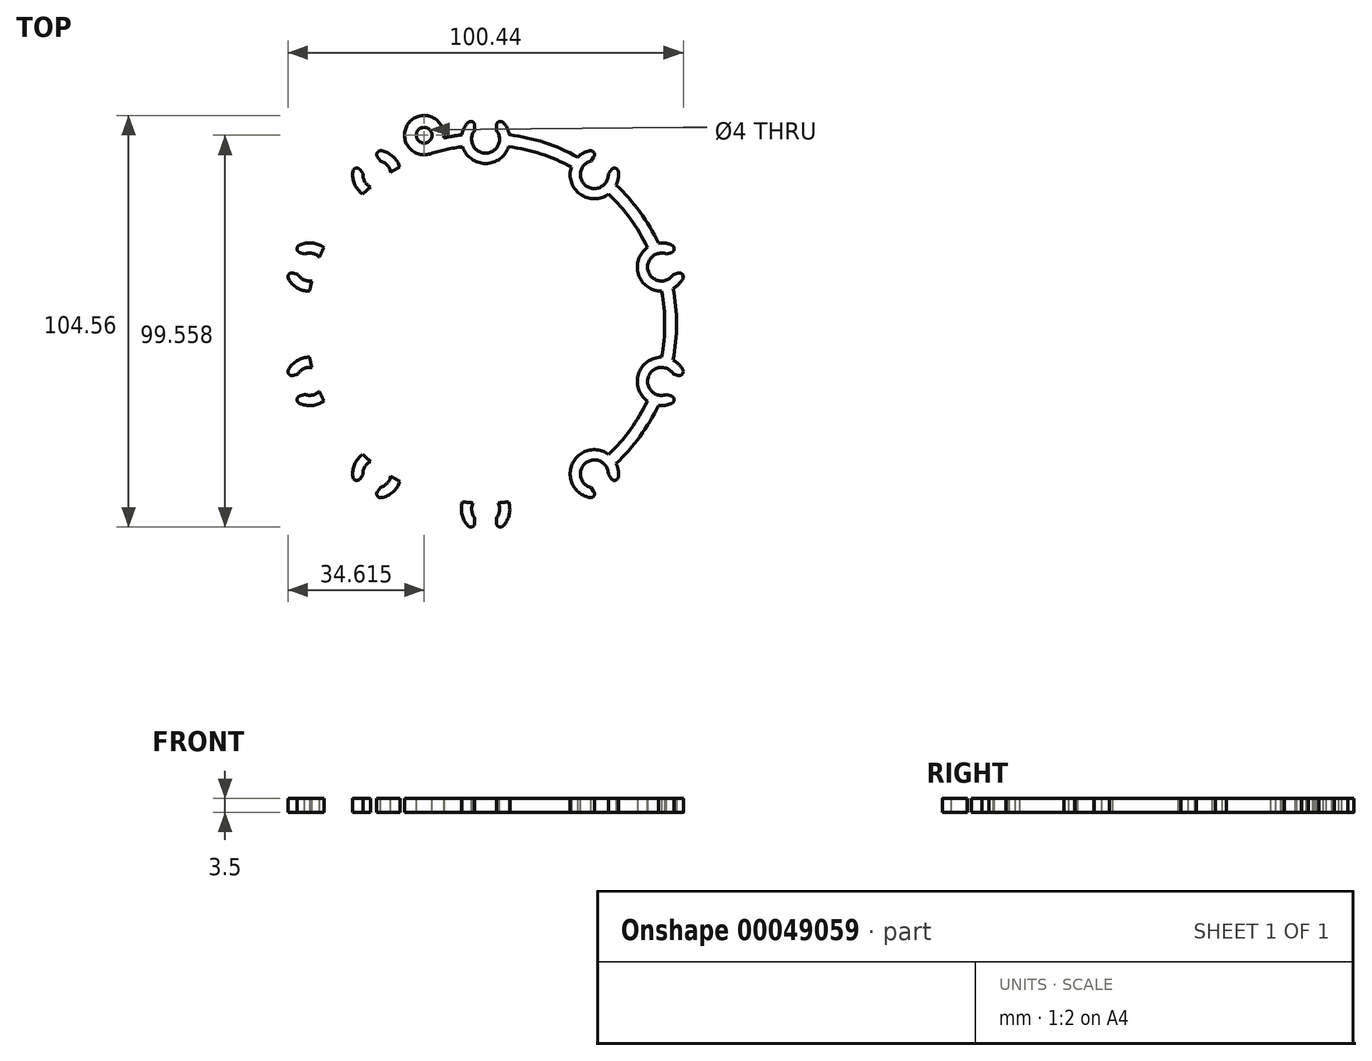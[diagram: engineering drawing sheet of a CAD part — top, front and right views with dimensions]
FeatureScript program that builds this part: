
annotation { "Feature Type Name" : "Feature", "Feature Type Description" : "" }
export const myFeature = defineFeature(function(context is Context, id is Id, definition is map)
    precondition{}
    {
        {
            var Q0;
            Q0=qCreatedBy(makeId("Top.planeOp"),FACE);
            var sketch = newSketch(context, id + "F0", { "sketchPlane" : qUnion([Q0])});
            skLineSegment(sketch, "E0", {"start": v(0, 0) * mm, "end": v(0, 47) * mm, "construction": true});
            skCircle(sketch, "E1", {"center": v(0, 47) * mm, "radius": 15 * mm, "construction": true});
            skCircle(sketch, "E2.1.0", {"center": v(-27.63, 38.02) * mm, "radius": 15 * mm, "construction": true});
            skCircle(sketch, "E2.2.0", {"center": v(-44.7, 14.52) * mm, "radius": 15 * mm, "construction": true});
            skCircle(sketch, "E2.3.0", {"center": v(-44.7, -14.52) * mm, "radius": 15 * mm, "construction": true});
            skCircle(sketch, "E2.4.0", {"center": v(-27.63, -38.02) * mm, "radius": 15 * mm, "construction": true});
            skCircle(sketch, "E2.5.0", {"center": v(0, -47) * mm, "radius": 15 * mm, "construction": true});
            skCircle(sketch, "E2.6.0", {"center": v(27.63, -38.02) * mm, "radius": 15 * mm, "construction": true});
            skCircle(sketch, "E2.7.0", {"center": v(44.7, -14.52) * mm, "radius": 15 * mm, "construction": true});
            skCircle(sketch, "E2.8.0", {"center": v(44.7, 14.52) * mm, "radius": 15 * mm, "construction": true});
            skCircle(sketch, "E2.9.0", {"center": v(27.63, 38.02) * mm, "radius": 15 * mm, "construction": true});
            skPoint(sketch, "E2.center", {"position": v(0, 0) * mm});
            skCircle(sketch, "E3", {"center": v(0, 47) * mm, "radius": 6.15 * mm});
            skCircle(sketch, "E4.1.0", {"center": v(-27.63, 38.02) * mm, "radius": 6.15 * mm});
            skCircle(sketch, "E4.2.0", {"center": v(-44.7, 14.52) * mm, "radius": 6.15 * mm});
            skCircle(sketch, "E4.3.0", {"center": v(-44.7, -14.52) * mm, "radius": 6.15 * mm});
            skCircle(sketch, "E4.4.0", {"center": v(-27.63, -38.02) * mm, "radius": 6.15 * mm});
            skCircle(sketch, "E4.5.0", {"center": v(0, -47) * mm, "radius": 6.15 * mm});
            skCircle(sketch, "E4.6.0", {"center": v(27.63, -38.02) * mm, "radius": 6.15 * mm});
            skCircle(sketch, "E4.7.0", {"center": v(44.7, -14.52) * mm, "radius": 6.15 * mm});
            skCircle(sketch, "E4.8.0", {"center": v(44.7, 14.52) * mm, "radius": 6.15 * mm});
            skCircle(sketch, "E4.9.0", {"center": v(27.63, 38.02) * mm, "radius": 6.15 * mm});
            skCircle(sketch, "E5", {"center": v(0, 0) * mm, "radius": 45.5 * mm});
            skCircle(sketch, "E6", {"center": v(0, 0) * mm, "radius": 48.5 * mm});
            skLineSegment(sketch, "E7", {"start": v(0, 0) * mm, "end": v(-15.6, 48.03) * mm, "construction": true});
            skCircle(sketch, "E8", {"center": v(-15.6, 48.03) * mm, "radius": 5 * mm});
            skSolve(sketch);
        }
        {
            var Q0;
            {var subQ0=sQuery(id+"F0.wireOp",EDGE,"E6");var subQ1=sQuery(id+"F0.wireOp",EDGE,"E4.2.0");var subQ3=makeQuery(id+"F0.imprint","INTERSECT",VERTEX,{"disambiguationData":[OD(0.0)],"derivedFrom":[subQ1,subQ0]});Q0=makeQuery(id+"F0.imprint","IMPRINT",FACE,{"disambiguationData":[TD([[makeQuery(id+"F0.imprint","IMPRINT",EDGE,{"disambiguationData":[TD([[subQ3,1.0]])],"derivedFrom":subQ1}),1.0]])]});}
            var Q1;
            {var subQ0=sQuery(id+"F0.wireOp",EDGE,"E6");var subQ1=sQuery(id+"F0.wireOp",EDGE,"E4.3.0");var subQ3=makeQuery(id+"F0.imprint","INTERSECT",VERTEX,{"disambiguationData":[OD(0.0)],"derivedFrom":[subQ1,subQ0]});Q1=makeQuery(id+"F0.imprint","IMPRINT",FACE,{"disambiguationData":[TD([[makeQuery(id+"F0.imprint","IMPRINT",EDGE,{"disambiguationData":[TD([[subQ3,1.0]])],"derivedFrom":subQ1}),1.0]])]});}
            var Q2;
            {var subQ1=sQuery(id+"F0.wireOp",EDGE,"E4.3.0");var subQ4=sQuery(id+"F0.wireOp",EDGE,"E6");var subQ6=makeQuery(id+"F0.imprint","INTERSECT",VERTEX,{"disambiguationData":[OD(0.0)],"derivedFrom":[subQ1,subQ4]});Q2=makeQuery(id+"F0.imprint","IMPRINT",FACE,{"disambiguationData":[TD([[makeQuery(id+"F0.imprint","IMPRINT",EDGE,{"disambiguationData":[TD([[subQ6,-1.0]])],"derivedFrom":subQ1}),1.0]])]});}
            var Q3;
            {var subQ3=sQuery(id+"F0.wireOp",EDGE,"E4.2.0");var subQ5=sQuery(id+"F0.wireOp",EDGE,"E6");var subQ7=makeQuery(id+"F0.imprint","INTERSECT",VERTEX,{"disambiguationData":[OD(0.0)],"derivedFrom":[subQ3,subQ5]});Q3=makeQuery(id+"F0.imprint","IMPRINT",FACE,{"disambiguationData":[TD([[makeQuery(id+"F0.imprint","IMPRINT",EDGE,{"disambiguationData":[TD([[subQ7,-1.0]])],"derivedFrom":subQ3}),-1.0]])]});}
            var Q4;
            {var subQ0=sQuery(id+"F0.wireOp",EDGE,"E5");var subQ1=sQuery(id+"F0.wireOp",EDGE,"E4.2.0");var subQ3=makeQuery(id+"F0.imprint","INTERSECT",VERTEX,{"disambiguationData":[OD(0.0)],"derivedFrom":[subQ1,subQ0]});Q4=makeQuery(id+"F0.imprint","IMPRINT",FACE,{"disambiguationData":[TD([[makeQuery(id+"F0.imprint","IMPRINT",EDGE,{"disambiguationData":[TD([[subQ3,-1.0]])],"derivedFrom":subQ1}),1.0]])]});}
            var Q5;
            {var subQ3=sQuery(id+"F0.wireOp",EDGE,"E4.3.0");var subQ5=sQuery(id+"F0.wireOp",EDGE,"E6");var subQ7=makeQuery(id+"F0.imprint","INTERSECT",VERTEX,{"disambiguationData":[OD(0.0)],"derivedFrom":[subQ3,subQ5]});Q5=makeQuery(id+"F0.imprint","IMPRINT",FACE,{"disambiguationData":[TD([[makeQuery(id+"F0.imprint","IMPRINT",EDGE,{"disambiguationData":[TD([[subQ7,-1.0]])],"derivedFrom":subQ3}),-1.0]])]});}
            var Q6;
            {var subQ0=sQuery(id+"F0.wireOp",EDGE,"E5");var subQ1=sQuery(id+"F0.wireOp",EDGE,"E4.4.0");var subQ3=makeQuery(id+"F0.imprint","INTERSECT",VERTEX,{"disambiguationData":[OD(0.0)],"derivedFrom":[subQ1,subQ0]});Q6=makeQuery(id+"F0.imprint","IMPRINT",FACE,{"disambiguationData":[TD([[makeQuery(id+"F0.imprint","IMPRINT",EDGE,{"disambiguationData":[TD([[subQ3,-1.0]])],"derivedFrom":subQ1}),1.0]])]});}
            var Q7;
            {var subQ0=sQuery(id+"F0.wireOp",EDGE,"E6");var subQ1=sQuery(id+"F0.wireOp",EDGE,"E4.4.0");var subQ3=makeQuery(id+"F0.imprint","INTERSECT",VERTEX,{"disambiguationData":[OD(0.0)],"derivedFrom":[subQ1,subQ0]});Q7=makeQuery(id+"F0.imprint","IMPRINT",FACE,{"disambiguationData":[TD([[makeQuery(id+"F0.imprint","IMPRINT",EDGE,{"disambiguationData":[TD([[subQ3,-1.0]])],"derivedFrom":subQ1}),1.0]])]});}
            var Q8;
            {var subQ0=sQuery(id+"F0.wireOp",EDGE,"E6");var subQ1=sQuery(id+"F0.wireOp",EDGE,"E4.4.0");var subQ3=makeQuery(id+"F0.imprint","INTERSECT",VERTEX,{"disambiguationData":[OD(0.0)],"derivedFrom":[subQ1,subQ0]});Q8=makeQuery(id+"F0.imprint","IMPRINT",FACE,{"disambiguationData":[TD([[makeQuery(id+"F0.imprint","IMPRINT",EDGE,{"disambiguationData":[TD([[subQ3,1.0]])],"derivedFrom":subQ1}),1.0]])]});}
            var Q9;
            {var subQ0=sQuery(id+"F0.wireOp",EDGE,"E6");var subQ3=sQuery(id+"F0.wireOp",EDGE,"E4.4.0");var subQ4=makeQuery(id+"F0.imprint","INTERSECT",VERTEX,{"disambiguationData":[OD(0.0)],"derivedFrom":[subQ3,subQ0]});Q9=makeQuery(id+"F0.imprint","IMPRINT",FACE,{"disambiguationData":[TD([[makeQuery(id+"F0.imprint","IMPRINT",EDGE,{"disambiguationData":[TD([[subQ4,-1.0]])],"derivedFrom":subQ3}),-1.0]])]});}
            var Q10;
            {var subQ0=sQuery(id+"F0.wireOp",EDGE,"E5");var subQ1=sQuery(id+"F0.wireOp",EDGE,"E4.5.0");var subQ3=makeQuery(id+"F0.imprint","INTERSECT",VERTEX,{"disambiguationData":[OD(0.0)],"derivedFrom":[subQ1,subQ0]});Q10=makeQuery(id+"F0.imprint","IMPRINT",FACE,{"disambiguationData":[TD([[makeQuery(id+"F0.imprint","IMPRINT",EDGE,{"disambiguationData":[TD([[subQ3,-1.0]])],"derivedFrom":subQ1}),1.0]])]});}
            var Q11;
            {var subQ0=sQuery(id+"F0.wireOp",EDGE,"E6");var subQ1=sQuery(id+"F0.wireOp",EDGE,"E4.5.0");var subQ3=makeQuery(id+"F0.imprint","INTERSECT",VERTEX,{"disambiguationData":[OD(0.0)],"derivedFrom":[subQ1,subQ0]});Q11=makeQuery(id+"F0.imprint","IMPRINT",FACE,{"disambiguationData":[TD([[makeQuery(id+"F0.imprint","IMPRINT",EDGE,{"disambiguationData":[TD([[subQ3,1.0]])],"derivedFrom":subQ1}),1.0]])]});}
            var Q12;
            {var subQ0=sQuery(id+"F0.wireOp",EDGE,"E6");var subQ1=sQuery(id+"F0.wireOp",EDGE,"E4.5.0");var subQ3=makeQuery(id+"F0.imprint","INTERSECT",VERTEX,{"disambiguationData":[OD(0.0)],"derivedFrom":[subQ1,subQ0]});Q12=makeQuery(id+"F0.imprint","IMPRINT",FACE,{"disambiguationData":[TD([[makeQuery(id+"F0.imprint","IMPRINT",EDGE,{"disambiguationData":[TD([[subQ3,-1.0]])],"derivedFrom":subQ1}),1.0]])]});}
            var Q13;
            {var subQ0=sQuery(id+"F0.wireOp",EDGE,"E6");var subQ3=sQuery(id+"F0.wireOp",EDGE,"E4.5.0");var subQ4=makeQuery(id+"F0.imprint","INTERSECT",VERTEX,{"disambiguationData":[OD(0.0)],"derivedFrom":[subQ3,subQ0]});Q13=makeQuery(id+"F0.imprint","IMPRINT",FACE,{"disambiguationData":[TD([[makeQuery(id+"F0.imprint","IMPRINT",EDGE,{"disambiguationData":[TD([[subQ4,-1.0]])],"derivedFrom":subQ3}),-1.0]])]});}
            var Q14;
            {var subQ0=sQuery(id+"F0.wireOp",EDGE,"E5");var subQ1=sQuery(id+"F0.wireOp",EDGE,"E4.6.0");var subQ3=makeQuery(id+"F0.imprint","INTERSECT",VERTEX,{"disambiguationData":[OD(0.0)],"derivedFrom":[subQ1,subQ0]});Q14=makeQuery(id+"F0.imprint","IMPRINT",FACE,{"disambiguationData":[TD([[makeQuery(id+"F0.imprint","IMPRINT",EDGE,{"disambiguationData":[TD([[subQ3,-1.0]])],"derivedFrom":subQ1}),1.0]])]});}
            var Q15;
            {var subQ0=sQuery(id+"F0.wireOp",EDGE,"E6");var subQ1=sQuery(id+"F0.wireOp",EDGE,"E4.6.0");var subQ3=makeQuery(id+"F0.imprint","INTERSECT",VERTEX,{"disambiguationData":[OD(0.0)],"derivedFrom":[subQ1,subQ0]});Q15=makeQuery(id+"F0.imprint","IMPRINT",FACE,{"disambiguationData":[TD([[makeQuery(id+"F0.imprint","IMPRINT",EDGE,{"disambiguationData":[TD([[subQ3,-1.0]])],"derivedFrom":subQ1}),1.0]])]});}
            var Q16;
            {var subQ0=sQuery(id+"F0.wireOp",EDGE,"E6");var subQ1=sQuery(id+"F0.wireOp",EDGE,"E4.6.0");var subQ3=makeQuery(id+"F0.imprint","INTERSECT",VERTEX,{"disambiguationData":[OD(0.0)],"derivedFrom":[subQ1,subQ0]});Q16=makeQuery(id+"F0.imprint","IMPRINT",FACE,{"disambiguationData":[TD([[makeQuery(id+"F0.imprint","IMPRINT",EDGE,{"disambiguationData":[TD([[subQ3,1.0]])],"derivedFrom":subQ1}),1.0]])]});}
            var Q17;
            {var subQ0=sQuery(id+"F0.wireOp",EDGE,"E6");var subQ3=sQuery(id+"F0.wireOp",EDGE,"E4.6.0");var subQ4=makeQuery(id+"F0.imprint","INTERSECT",VERTEX,{"disambiguationData":[OD(0.0)],"derivedFrom":[subQ3,subQ0]});Q17=makeQuery(id+"F0.imprint","IMPRINT",FACE,{"disambiguationData":[TD([[makeQuery(id+"F0.imprint","IMPRINT",EDGE,{"disambiguationData":[TD([[subQ4,-1.0]])],"derivedFrom":subQ3}),-1.0]])]});}
            var Q18;
            {var subQ0=sQuery(id+"F0.wireOp",EDGE,"E5");var subQ1=sQuery(id+"F0.wireOp",EDGE,"E4.7.0");var subQ3=makeQuery(id+"F0.imprint","INTERSECT",VERTEX,{"disambiguationData":[OD(0.0)],"derivedFrom":[subQ1,subQ0]});Q18=makeQuery(id+"F0.imprint","IMPRINT",FACE,{"disambiguationData":[TD([[makeQuery(id+"F0.imprint","IMPRINT",EDGE,{"disambiguationData":[TD([[subQ3,-1.0]])],"derivedFrom":subQ1}),1.0]])]});}
            var Q19;
            {var subQ0=sQuery(id+"F0.wireOp",EDGE,"E6");var subQ1=sQuery(id+"F0.wireOp",EDGE,"E4.7.0");var subQ3=makeQuery(id+"F0.imprint","INTERSECT",VERTEX,{"disambiguationData":[OD(0.0)],"derivedFrom":[subQ1,subQ0]});Q19=makeQuery(id+"F0.imprint","IMPRINT",FACE,{"disambiguationData":[TD([[makeQuery(id+"F0.imprint","IMPRINT",EDGE,{"disambiguationData":[TD([[subQ3,-1.0]])],"derivedFrom":subQ1}),1.0]])]});}
            var Q20;
            {var subQ0=sQuery(id+"F0.wireOp",EDGE,"E6");var subQ1=sQuery(id+"F0.wireOp",EDGE,"E4.7.0");var subQ3=makeQuery(id+"F0.imprint","INTERSECT",VERTEX,{"disambiguationData":[OD(0.0)],"derivedFrom":[subQ1,subQ0]});Q20=makeQuery(id+"F0.imprint","IMPRINT",FACE,{"disambiguationData":[TD([[makeQuery(id+"F0.imprint","IMPRINT",EDGE,{"disambiguationData":[TD([[subQ3,1.0]])],"derivedFrom":subQ1}),1.0]])]});}
            var Q21;
            {var subQ0=sQuery(id+"F0.wireOp",EDGE,"E6");var subQ3=sQuery(id+"F0.wireOp",EDGE,"E4.7.0");var subQ4=makeQuery(id+"F0.imprint","INTERSECT",VERTEX,{"disambiguationData":[OD(0.0)],"derivedFrom":[subQ3,subQ0]});Q21=makeQuery(id+"F0.imprint","IMPRINT",FACE,{"disambiguationData":[TD([[makeQuery(id+"F0.imprint","IMPRINT",EDGE,{"disambiguationData":[TD([[subQ4,-1.0]])],"derivedFrom":subQ3}),-1.0]])]});}
            var Q22;
            {var subQ0=sQuery(id+"F0.wireOp",EDGE,"E5");var subQ1=sQuery(id+"F0.wireOp",EDGE,"E4.8.0");var subQ3=makeQuery(id+"F0.imprint","INTERSECT",VERTEX,{"disambiguationData":[OD(0.0)],"derivedFrom":[subQ1,subQ0]});Q22=makeQuery(id+"F0.imprint","IMPRINT",FACE,{"disambiguationData":[TD([[makeQuery(id+"F0.imprint","IMPRINT",EDGE,{"disambiguationData":[TD([[subQ3,-1.0]])],"derivedFrom":subQ1}),1.0]])]});}
            var Q23;
            {var subQ0=sQuery(id+"F0.wireOp",EDGE,"E6");var subQ1=sQuery(id+"F0.wireOp",EDGE,"E4.8.0");var subQ3=makeQuery(id+"F0.imprint","INTERSECT",VERTEX,{"disambiguationData":[OD(0.0)],"derivedFrom":[subQ1,subQ0]});Q23=makeQuery(id+"F0.imprint","IMPRINT",FACE,{"disambiguationData":[TD([[makeQuery(id+"F0.imprint","IMPRINT",EDGE,{"disambiguationData":[TD([[subQ3,1.0]])],"derivedFrom":subQ1}),1.0]])]});}
            var Q24;
            {var subQ0=sQuery(id+"F0.wireOp",EDGE,"E6");var subQ1=sQuery(id+"F0.wireOp",EDGE,"E4.2.0");var subQ3=makeQuery(id+"F0.imprint","INTERSECT",VERTEX,{"disambiguationData":[OD(0.0)],"derivedFrom":[subQ1,subQ0]});Q24=makeQuery(id+"F0.imprint","IMPRINT",FACE,{"disambiguationData":[TD([[makeQuery(id+"F0.imprint","IMPRINT",EDGE,{"disambiguationData":[TD([[subQ3,-1.0]])],"derivedFrom":subQ1}),1.0]])]});}
            var Q25;
            {var subQ0=sQuery(id+"F0.wireOp",EDGE,"E6");var subQ3=sQuery(id+"F0.wireOp",EDGE,"E4.1.0");var subQ4=makeQuery(id+"F0.imprint","INTERSECT",VERTEX,{"disambiguationData":[OD(0.0)],"derivedFrom":[subQ3,subQ0]});Q25=makeQuery(id+"F0.imprint","IMPRINT",FACE,{"disambiguationData":[TD([[makeQuery(id+"F0.imprint","IMPRINT",EDGE,{"disambiguationData":[TD([[subQ4,-1.0]])],"derivedFrom":subQ3}),-1.0]])]});}
            var Q26;
            {var subQ0=sQuery(id+"F0.wireOp",EDGE,"E6");var subQ1=sQuery(id+"F0.wireOp",EDGE,"E4.1.0");var subQ3=makeQuery(id+"F0.imprint","INTERSECT",VERTEX,{"disambiguationData":[OD(0.0)],"derivedFrom":[subQ1,subQ0]});Q26=makeQuery(id+"F0.imprint","IMPRINT",FACE,{"disambiguationData":[TD([[makeQuery(id+"F0.imprint","IMPRINT",EDGE,{"disambiguationData":[TD([[subQ3,1.0]])],"derivedFrom":subQ1}),1.0]])]});}
            var Q27;
            {var subQ0=sQuery(id+"F0.wireOp",EDGE,"E6");var subQ1=sQuery(id+"F0.wireOp",EDGE,"E4.1.0");var subQ3=makeQuery(id+"F0.imprint","INTERSECT",VERTEX,{"disambiguationData":[OD(0.0)],"derivedFrom":[subQ1,subQ0]});Q27=makeQuery(id+"F0.imprint","IMPRINT",FACE,{"disambiguationData":[TD([[makeQuery(id+"F0.imprint","IMPRINT",EDGE,{"disambiguationData":[TD([[subQ3,-1.0]])],"derivedFrom":subQ1}),1.0]])]});}
            var Q28;
            {var subQ0=sQuery(id+"F0.wireOp",EDGE,"E5");var subQ1=sQuery(id+"F0.wireOp",EDGE,"E4.1.0");var subQ3=makeQuery(id+"F0.imprint","INTERSECT",VERTEX,{"disambiguationData":[OD(0.0)],"derivedFrom":[subQ1,subQ0]});Q28=makeQuery(id+"F0.imprint","IMPRINT",FACE,{"disambiguationData":[TD([[makeQuery(id+"F0.imprint","IMPRINT",EDGE,{"disambiguationData":[TD([[subQ3,-1.0]])],"derivedFrom":subQ1}),1.0]])]});}
            var Q29;
            {var subQ3=sQuery(id+"F0.wireOp",EDGE,"E6");var subQ5=sQuery(id+"F0.wireOp",EDGE,"E4.1.0");var subQ6=makeQuery(id+"F0.imprint","INTERSECT",VERTEX,{"disambiguationData":[OD(1.0)],"derivedFrom":[subQ5,subQ3]});Q29=makeQuery(id+"F0.imprint","IMPRINT",FACE,{"disambiguationData":[TD([[makeQuery(id+"F0.imprint","IMPRINT",EDGE,{"disambiguationData":[TD([[subQ6,1.0]])],"derivedFrom":subQ5}),-1.0]])]});}
            var Q30;
            {var subQ0=sQuery(id+"F0.wireOp",EDGE,"E6");var subQ3=sQuery(id+"F0.wireOp",EDGE,"E3");var subQ4=makeQuery(id+"F0.imprint","INTERSECT",VERTEX,{"disambiguationData":[OD(0.0)],"derivedFrom":[subQ3,subQ0]});Q30=makeQuery(id+"F0.imprint","IMPRINT",FACE,{"disambiguationData":[TD([[makeQuery(id+"F0.imprint","IMPRINT",EDGE,{"disambiguationData":[TD([[subQ4,-1.0]])],"derivedFrom":subQ3}),-1.0]])]});}
            var Q31;
            {var subQ0=sQuery(id+"F0.wireOp",EDGE,"E8");var subQ2=sQuery(id+"F0.wireOp",EDGE,"E6");var subQ3=makeQuery(id+"F0.imprint","INTERSECT",VERTEX,{"disambiguationData":[OD(0.0)],"derivedFrom":[subQ2,subQ0]});Q31=makeQuery(id+"F0.imprint","IMPRINT",FACE,{"disambiguationData":[TD([[makeQuery(id+"F0.imprint","IMPRINT",EDGE,{"disambiguationData":[TD([[subQ3,-1.0]])],"derivedFrom":subQ2}),1.0]])]});}
            var Q32;
            {var subQ0=sQuery(id+"F0.wireOp",EDGE,"E8");var subQ1=sQuery(id+"F0.wireOp",EDGE,"E6");var subQ3=makeQuery(id+"F0.imprint","INTERSECT",VERTEX,{"disambiguationData":[OD(0.0)],"derivedFrom":[subQ1,subQ0]});Q32=makeQuery(id+"F0.imprint","IMPRINT",FACE,{"disambiguationData":[TD([[makeQuery(id+"F0.imprint","IMPRINT",EDGE,{"disambiguationData":[TD([[subQ3,-1.0]])],"derivedFrom":subQ1}),-1.0]])]});}
            var Q33;
            {var subQ0=sQuery(id+"F0.wireOp",EDGE,"E5");var subQ1=sQuery(id+"F0.wireOp",EDGE,"E3");var subQ3=makeQuery(id+"F0.imprint","INTERSECT",VERTEX,{"disambiguationData":[OD(0.0)],"derivedFrom":[subQ1,subQ0]});Q33=makeQuery(id+"F0.imprint","IMPRINT",FACE,{"disambiguationData":[TD([[makeQuery(id+"F0.imprint","IMPRINT",EDGE,{"disambiguationData":[TD([[subQ3,-1.0]])],"derivedFrom":subQ1}),1.0]])]});}
            var Q34;
            {var subQ0=sQuery(id+"F0.wireOp",EDGE,"E6");var subQ1=sQuery(id+"F0.wireOp",EDGE,"E3");var subQ3=makeQuery(id+"F0.imprint","INTERSECT",VERTEX,{"disambiguationData":[OD(0.0)],"derivedFrom":[subQ1,subQ0]});Q34=makeQuery(id+"F0.imprint","IMPRINT",FACE,{"disambiguationData":[TD([[makeQuery(id+"F0.imprint","IMPRINT",EDGE,{"disambiguationData":[TD([[subQ3,-1.0]])],"derivedFrom":subQ1}),1.0]])]});}
            var Q35;
            {var subQ0=sQuery(id+"F0.wireOp",EDGE,"E6");var subQ1=sQuery(id+"F0.wireOp",EDGE,"E3");var subQ3=makeQuery(id+"F0.imprint","INTERSECT",VERTEX,{"disambiguationData":[OD(0.0)],"derivedFrom":[subQ1,subQ0]});Q35=makeQuery(id+"F0.imprint","IMPRINT",FACE,{"disambiguationData":[TD([[makeQuery(id+"F0.imprint","IMPRINT",EDGE,{"disambiguationData":[TD([[subQ3,1.0]])],"derivedFrom":subQ1}),1.0]])]});}
            var Q36;
            {var subQ3=sQuery(id+"F0.wireOp",EDGE,"E3");var subQ5=sQuery(id+"F0.wireOp",EDGE,"E6");var subQ7=makeQuery(id+"F0.imprint","INTERSECT",VERTEX,{"disambiguationData":[OD(1.0)],"derivedFrom":[subQ3,subQ5]});Q36=makeQuery(id+"F0.imprint","IMPRINT",FACE,{"disambiguationData":[TD([[makeQuery(id+"F0.imprint","IMPRINT",EDGE,{"disambiguationData":[TD([[subQ7,1.0]])],"derivedFrom":subQ3}),-1.0]])]});}
            var Q37;
            {var subQ0=sQuery(id+"F0.wireOp",EDGE,"E6");var subQ1=sQuery(id+"F0.wireOp",EDGE,"E4.9.0");var subQ3=makeQuery(id+"F0.imprint","INTERSECT",VERTEX,{"disambiguationData":[OD(0.0)],"derivedFrom":[subQ1,subQ0]});Q37=makeQuery(id+"F0.imprint","IMPRINT",FACE,{"disambiguationData":[TD([[makeQuery(id+"F0.imprint","IMPRINT",EDGE,{"disambiguationData":[TD([[subQ3,1.0]])],"derivedFrom":subQ1}),1.0]])]});}
            var Q38;
            {var subQ0=sQuery(id+"F0.wireOp",EDGE,"E6");var subQ1=sQuery(id+"F0.wireOp",EDGE,"E4.9.0");var subQ3=makeQuery(id+"F0.imprint","INTERSECT",VERTEX,{"disambiguationData":[OD(0.0)],"derivedFrom":[subQ1,subQ0]});Q38=makeQuery(id+"F0.imprint","IMPRINT",FACE,{"disambiguationData":[TD([[makeQuery(id+"F0.imprint","IMPRINT",EDGE,{"disambiguationData":[TD([[subQ3,-1.0]])],"derivedFrom":subQ1}),1.0]])]});}
            var Q39;
            {var subQ0=sQuery(id+"F0.wireOp",EDGE,"E5");var subQ1=sQuery(id+"F0.wireOp",EDGE,"E4.9.0");var subQ3=makeQuery(id+"F0.imprint","INTERSECT",VERTEX,{"disambiguationData":[OD(0.0)],"derivedFrom":[subQ1,subQ0]});Q39=makeQuery(id+"F0.imprint","IMPRINT",FACE,{"disambiguationData":[TD([[makeQuery(id+"F0.imprint","IMPRINT",EDGE,{"disambiguationData":[TD([[subQ3,-1.0]])],"derivedFrom":subQ1}),1.0]])]});}
            var Q40;
            {var subQ0=sQuery(id+"F0.wireOp",EDGE,"E6");var subQ3=sQuery(id+"F0.wireOp",EDGE,"E4.8.0");var subQ4=makeQuery(id+"F0.imprint","INTERSECT",VERTEX,{"disambiguationData":[OD(0.0)],"derivedFrom":[subQ3,subQ0]});Q40=makeQuery(id+"F0.imprint","IMPRINT",FACE,{"disambiguationData":[TD([[makeQuery(id+"F0.imprint","IMPRINT",EDGE,{"disambiguationData":[TD([[subQ4,-1.0]])],"derivedFrom":subQ3}),-1.0]])]});}
            var Q41;
            {var subQ0=sQuery(id+"F0.wireOp",EDGE,"E6");var subQ1=sQuery(id+"F0.wireOp",EDGE,"E4.8.0");var subQ3=makeQuery(id+"F0.imprint","INTERSECT",VERTEX,{"disambiguationData":[OD(0.0)],"derivedFrom":[subQ1,subQ0]});Q41=makeQuery(id+"F0.imprint","IMPRINT",FACE,{"disambiguationData":[TD([[makeQuery(id+"F0.imprint","IMPRINT",EDGE,{"disambiguationData":[TD([[subQ3,-1.0]])],"derivedFrom":subQ1}),1.0]])]});}
            var Q42;
            {var subQ0=sQuery(id+"F0.wireOp",EDGE,"E5");var subQ1=sQuery(id+"F0.wireOp",EDGE,"E4.3.0");var subQ3=makeQuery(id+"F0.imprint","INTERSECT",VERTEX,{"disambiguationData":[OD(0.0)],"derivedFrom":[subQ1,subQ0]});Q42=makeQuery(id+"F0.imprint","IMPRINT",FACE,{"disambiguationData":[TD([[makeQuery(id+"F0.imprint","IMPRINT",EDGE,{"disambiguationData":[TD([[subQ3,-1.0]])],"derivedFrom":subQ1}),1.0]])]});}
            extrude(context, id + "F1", {"entities" : qUnion([Q0, Q1, Q2, Q3, Q4, Q5, Q6, Q7, Q8, Q9, Q10, Q11, Q12, Q13, Q14, Q15, Q16, Q17, Q18, Q19, Q20, Q21, Q22, Q23, Q24, Q25, Q26, Q27, Q28, Q29, Q30, Q31, Q32, Q33, Q34, Q35, Q36, Q37, Q38, Q39, Q40, Q41, Q42]), "depth" : 3.5 * mm});
        }
        {
            var Q0;
            Q0=makeQuery(id+"F1.opExtrude","CAP_FACE",FACE,{"disambiguationData":[OSD([sQuery(id+"F0.wireOp",EDGE,"E3"),sQuery(id+"F0.wireOp",EDGE,"E4.1.0"),sQuery(id+"F0.wireOp",EDGE,"E4.2.0"),sQuery(id+"F0.wireOp",EDGE,"E4.3.0"),sQuery(id+"F0.wireOp",EDGE,"E4.4.0"),sQuery(id+"F0.wireOp",EDGE,"E4.5.0"),sQuery(id+"F0.wireOp",EDGE,"E4.6.0"),sQuery(id+"F0.wireOp",EDGE,"E4.7.0"),sQuery(id+"F0.wireOp",EDGE,"E4.8.0"),sQuery(id+"F0.wireOp",EDGE,"E4.9.0"),sQuery(id+"F0.wireOp",EDGE,"E5"),sQuery(id+"F0.wireOp",EDGE,"E6"),sQuery(id+"F0.wireOp",EDGE,"E8")])],"isStart":false});
            var sketch = newSketch(context, id + "F2", { "sketchPlane" : qUnion([Q0])});
            skCircle(sketch, "E9", {"center": v(0, 47) * mm, "radius": 3.55 * mm});
            skCircle(sketch, "E10.1.0", {"center": v(-27.63, 38.02) * mm, "radius": 3.55 * mm});
            skCircle(sketch, "E10.2.0", {"center": v(-44.7, 14.52) * mm, "radius": 3.55 * mm});
            skCircle(sketch, "E10.3.0", {"center": v(-44.7, -14.52) * mm, "radius": 3.55 * mm});
            skCircle(sketch, "E10.4.0", {"center": v(-27.63, -38.02) * mm, "radius": 3.55 * mm});
            skCircle(sketch, "E10.5.0", {"center": v(0, -47) * mm, "radius": 3.55 * mm});
            skCircle(sketch, "E10.6.0", {"center": v(27.63, -38.02) * mm, "radius": 3.55 * mm});
            skCircle(sketch, "E10.7.0", {"center": v(44.7, -14.52) * mm, "radius": 3.55 * mm});
            skCircle(sketch, "E10.8.0", {"center": v(44.7, 14.52) * mm, "radius": 3.55 * mm});
            skCircle(sketch, "E10.9.0", {"center": v(27.63, 38.02) * mm, "radius": 3.55 * mm});
            skPoint(sketch, "E10.center", {"position": v(0, 0) * mm});
            skCircle(sketch, "E11", {"center": v(-15.6, 48.03) * mm, "radius": 2 * mm});
            skLineSegment(sketch, "E12", {"start": v(0, 59.46) * mm, "end": v(-2.75, 59.46) * mm, "construction": true});
            skLineSegment(sketch, "E13.bottom", {"start": v(-2.75, 59.46) * mm, "end": v(2.75, 59.46) * mm});
            skLineSegment(sketch, "E13.top", {"start": v(-2.75, 47) * mm, "end": v(2.75, 47) * mm});
            skLineSegment(sketch, "E13.left", {"start": v(-2.75, 59.46) * mm, "end": v(-2.75, 47) * mm});
            skLineSegment(sketch, "E13.right", {"start": v(2.75, 59.46) * mm, "end": v(2.75, 47) * mm});
            skLineSegment(sketch, "E14.1.0", {"start": v(-37.18, 46.49) * mm, "end": v(-29.85, 36.41) * mm});
            skLineSegment(sketch, "E14.1.1", {"start": v(-32.73, 49.72) * mm, "end": v(-25.4, 39.64) * mm});
            skLineSegment(sketch, "E14.1.2", {"start": v(-37.18, 46.49) * mm, "end": v(-32.73, 49.72) * mm});
            skLineSegment(sketch, "E14.2.0", {"start": v(-57.4, 15.76) * mm, "end": v(-45.55, 11.9) * mm});
            skLineSegment(sketch, "E14.2.1", {"start": v(-55.7, 21) * mm, "end": v(-43.85, 17.14) * mm});
            skLineSegment(sketch, "E14.2.2", {"start": v(-57.4, 15.76) * mm, "end": v(-55.7, 21) * mm});
            skLineSegment(sketch, "E14.3.0", {"start": v(-55.7, -21) * mm, "end": v(-43.85, -17.14) * mm});
            skLineSegment(sketch, "E14.3.1", {"start": v(-57.4, -15.76) * mm, "end": v(-45.55, -11.9) * mm});
            skLineSegment(sketch, "E14.3.2", {"start": v(-55.7, -21) * mm, "end": v(-57.4, -15.76) * mm});
            skLineSegment(sketch, "E14.4.0", {"start": v(-32.73, -49.72) * mm, "end": v(-25.4, -39.64) * mm});
            skLineSegment(sketch, "E14.4.1", {"start": v(-37.18, -46.49) * mm, "end": v(-29.85, -36.41) * mm});
            skLineSegment(sketch, "E14.4.2", {"start": v(-32.73, -49.72) * mm, "end": v(-37.18, -46.49) * mm});
            skLineSegment(sketch, "E14.5.0", {"start": v(2.75, -59.46) * mm, "end": v(2.75, -47) * mm});
            skLineSegment(sketch, "E14.5.1", {"start": v(-2.75, -59.46) * mm, "end": v(-2.75, -47) * mm});
            skLineSegment(sketch, "E14.5.2", {"start": v(2.75, -59.46) * mm, "end": v(-2.75, -59.46) * mm});
            skLineSegment(sketch, "E14.6.0", {"start": v(37.18, -46.49) * mm, "end": v(29.85, -36.41) * mm});
            skLineSegment(sketch, "E14.6.1", {"start": v(32.73, -49.72) * mm, "end": v(25.4, -39.64) * mm});
            skLineSegment(sketch, "E14.6.2", {"start": v(37.18, -46.49) * mm, "end": v(32.73, -49.72) * mm});
            skLineSegment(sketch, "E14.7.0", {"start": v(57.4, -15.76) * mm, "end": v(45.55, -11.9) * mm});
            skLineSegment(sketch, "E14.7.1", {"start": v(55.7, -21) * mm, "end": v(43.85, -17.14) * mm});
            skLineSegment(sketch, "E14.7.2", {"start": v(57.4, -15.76) * mm, "end": v(55.7, -21) * mm});
            skLineSegment(sketch, "E14.8.0", {"start": v(55.7, 21) * mm, "end": v(43.85, 17.14) * mm});
            skLineSegment(sketch, "E14.8.1", {"start": v(57.4, 15.76) * mm, "end": v(45.55, 11.9) * mm});
            skLineSegment(sketch, "E14.8.2", {"start": v(55.7, 21) * mm, "end": v(57.4, 15.76) * mm});
            skLineSegment(sketch, "E14.9.0", {"start": v(32.73, 49.72) * mm, "end": v(25.4, 39.64) * mm});
            skLineSegment(sketch, "E14.9.1", {"start": v(37.18, 46.49) * mm, "end": v(29.85, 36.41) * mm});
            skLineSegment(sketch, "E14.9.2", {"start": v(32.73, 49.72) * mm, "end": v(37.18, 46.49) * mm});
            skSolve(sketch);
        }
        {
            var Q0;
            Q0 = qSketchRegion(id + "F2", true);
            extrude(context, id + "F3", {"entities" : qUnion([Q0]), "operationType" : NewBodyOperationType.REMOVE, "oppositeDirection" : true, "depth" : 25 * mm});
        }
        {
            var Q0;
            {var subQ0=sQuery(id+"F0.wireOp",EDGE,"E4.3.0");var subQ1=sQuery(id+"F0.wireOp",EDGE,"E6");Q0=makeQuery(id+"F3.boolean.opBoolean","INTERSECT",EDGE,{"derivedFrom":[makeQuery(id+"F1.opExtrude","SWEPT_FACE",FACE,{"disambiguationData":[OSD([subQ0]),TDD([makeQuery(id+"F0.imprint","IMPRINT",EDGE,{"disambiguationData":[TD([[makeQuery(id+"F0.imprint","INTERSECT",VERTEX,{"disambiguationData":[OD(0.0)],"derivedFrom":[subQ0,subQ1]}),1.0]])],"derivedFrom":subQ0})])]}),makeQuery(id+"F3.opExtrude","SWEPT_FACE",FACE,{"disambiguationData":[OSD([sQuery(id+"F2.wireOp",EDGE,"E14.3.0")])]})]});}
            var Q1;
            {var subQ0=sQuery(id+"F0.wireOp",EDGE,"E4.3.0");var subQ1=sQuery(id+"F0.wireOp",EDGE,"E6");Q1=makeQuery(id+"F3.boolean.opBoolean","INTERSECT",EDGE,{"derivedFrom":[makeQuery(id+"F1.opExtrude","SWEPT_FACE",FACE,{"disambiguationData":[OSD([subQ0]),TDD([makeQuery(id+"F0.imprint","IMPRINT",EDGE,{"disambiguationData":[TD([[makeQuery(id+"F0.imprint","INTERSECT",VERTEX,{"disambiguationData":[OD(0.0)],"derivedFrom":[subQ0,subQ1]}),1.0]])],"derivedFrom":subQ0})])]}),makeQuery(id+"F3.opExtrude","SWEPT_FACE",FACE,{"disambiguationData":[OSD([sQuery(id+"F2.wireOp",EDGE,"E14.3.1")])]})]});}
            var Q2;
            {var subQ0=sQuery(id+"F0.wireOp",EDGE,"E4.4.0");var subQ1=sQuery(id+"F0.wireOp",EDGE,"E6");Q2=makeQuery(id+"F3.boolean.opBoolean","INTERSECT",EDGE,{"derivedFrom":[makeQuery(id+"F1.opExtrude","SWEPT_FACE",FACE,{"disambiguationData":[OSD([subQ0]),TDD([makeQuery(id+"F0.imprint","IMPRINT",EDGE,{"disambiguationData":[TD([[makeQuery(id+"F0.imprint","INTERSECT",VERTEX,{"disambiguationData":[OD(0.0)],"derivedFrom":[subQ0,subQ1]}),1.0]])],"derivedFrom":subQ0})])]}),makeQuery(id+"F3.opExtrude","SWEPT_FACE",FACE,{"disambiguationData":[OSD([sQuery(id+"F2.wireOp",EDGE,"E14.4.1")])]})]});}
            var Q3;
            {var subQ0=sQuery(id+"F0.wireOp",EDGE,"E4.4.0");var subQ1=sQuery(id+"F0.wireOp",EDGE,"E6");Q3=makeQuery(id+"F3.boolean.opBoolean","INTERSECT",EDGE,{"derivedFrom":[makeQuery(id+"F1.opExtrude","SWEPT_FACE",FACE,{"disambiguationData":[OSD([subQ0]),TDD([makeQuery(id+"F0.imprint","IMPRINT",EDGE,{"disambiguationData":[TD([[makeQuery(id+"F0.imprint","INTERSECT",VERTEX,{"disambiguationData":[OD(0.0)],"derivedFrom":[subQ0,subQ1]}),1.0]])],"derivedFrom":subQ0})])]}),makeQuery(id+"F3.opExtrude","SWEPT_FACE",FACE,{"disambiguationData":[OSD([sQuery(id+"F2.wireOp",EDGE,"E14.4.0")])]})]});}
            var Q4;
            {var subQ0=sQuery(id+"F0.wireOp",EDGE,"E4.5.0");var subQ1=sQuery(id+"F0.wireOp",EDGE,"E6");Q4=makeQuery(id+"F3.boolean.opBoolean","INTERSECT",EDGE,{"derivedFrom":[makeQuery(id+"F1.opExtrude","SWEPT_FACE",FACE,{"disambiguationData":[OSD([subQ0]),TDD([makeQuery(id+"F0.imprint","IMPRINT",EDGE,{"disambiguationData":[TD([[makeQuery(id+"F0.imprint","INTERSECT",VERTEX,{"disambiguationData":[OD(0.0)],"derivedFrom":[subQ0,subQ1]}),1.0]])],"derivedFrom":subQ0})])]}),makeQuery(id+"F3.opExtrude","SWEPT_FACE",FACE,{"disambiguationData":[OSD([sQuery(id+"F2.wireOp",EDGE,"E14.5.1")])]})]});}
            var Q5;
            {var subQ0=sQuery(id+"F0.wireOp",EDGE,"E4.5.0");var subQ1=sQuery(id+"F0.wireOp",EDGE,"E6");Q5=makeQuery(id+"F3.boolean.opBoolean","INTERSECT",EDGE,{"derivedFrom":[makeQuery(id+"F1.opExtrude","SWEPT_FACE",FACE,{"disambiguationData":[OSD([subQ0]),TDD([makeQuery(id+"F0.imprint","IMPRINT",EDGE,{"disambiguationData":[TD([[makeQuery(id+"F0.imprint","INTERSECT",VERTEX,{"disambiguationData":[OD(0.0)],"derivedFrom":[subQ0,subQ1]}),1.0]])],"derivedFrom":subQ0})])]}),makeQuery(id+"F3.opExtrude","SWEPT_FACE",FACE,{"disambiguationData":[OSD([sQuery(id+"F2.wireOp",EDGE,"E14.5.0")])]})]});}
            var Q6;
            {var subQ0=sQuery(id+"F0.wireOp",EDGE,"E4.2.0");var subQ1=sQuery(id+"F0.wireOp",EDGE,"E6");Q6=makeQuery(id+"F3.boolean.opBoolean","INTERSECT",EDGE,{"derivedFrom":[makeQuery(id+"F1.opExtrude","SWEPT_FACE",FACE,{"disambiguationData":[OSD([subQ0]),TDD([makeQuery(id+"F0.imprint","IMPRINT",EDGE,{"disambiguationData":[TD([[makeQuery(id+"F0.imprint","INTERSECT",VERTEX,{"disambiguationData":[OD(0.0)],"derivedFrom":[subQ0,subQ1]}),1.0]])],"derivedFrom":subQ0})])]}),makeQuery(id+"F3.opExtrude","SWEPT_FACE",FACE,{"disambiguationData":[OSD([sQuery(id+"F2.wireOp",EDGE,"E14.2.1")])]})]});}
            var Q7;
            {var subQ0=sQuery(id+"F0.wireOp",EDGE,"E4.1.0");var subQ1=sQuery(id+"F0.wireOp",EDGE,"E6");Q7=makeQuery(id+"F3.boolean.opBoolean","INTERSECT",EDGE,{"derivedFrom":[makeQuery(id+"F1.opExtrude","SWEPT_FACE",FACE,{"disambiguationData":[OSD([subQ0]),TDD([makeQuery(id+"F0.imprint","IMPRINT",EDGE,{"disambiguationData":[TD([[makeQuery(id+"F0.imprint","INTERSECT",VERTEX,{"disambiguationData":[OD(0.0)],"derivedFrom":[subQ0,subQ1]}),1.0]])],"derivedFrom":subQ0})])]}),makeQuery(id+"F3.opExtrude","SWEPT_FACE",FACE,{"disambiguationData":[OSD([sQuery(id+"F2.wireOp",EDGE,"E14.1.1")])]})]});}
            var Q8;
            {var subQ0=sQuery(id+"F0.wireOp",EDGE,"E3");var subQ1=sQuery(id+"F0.wireOp",EDGE,"E6");Q8=makeQuery(id+"F3.boolean.opBoolean","INTERSECT",EDGE,{"derivedFrom":[makeQuery(id+"F1.opExtrude","SWEPT_FACE",FACE,{"disambiguationData":[OSD([subQ0]),TDD([makeQuery(id+"F0.imprint","IMPRINT",EDGE,{"disambiguationData":[TD([[makeQuery(id+"F0.imprint","INTERSECT",VERTEX,{"disambiguationData":[OD(0.0)],"derivedFrom":[subQ0,subQ1]}),1.0]])],"derivedFrom":subQ0})])]}),makeQuery(id+"F3.opExtrude","SWEPT_FACE",FACE,{"disambiguationData":[OSD([sQuery(id+"F2.wireOp",EDGE,"E13.right")])]})]});}
            var Q9;
            {var subQ0=sQuery(id+"F0.wireOp",EDGE,"E4.9.0");var subQ1=sQuery(id+"F0.wireOp",EDGE,"E6");Q9=makeQuery(id+"F3.boolean.opBoolean","INTERSECT",EDGE,{"derivedFrom":[makeQuery(id+"F1.opExtrude","SWEPT_FACE",FACE,{"disambiguationData":[OSD([subQ0]),TDD([makeQuery(id+"F0.imprint","IMPRINT",EDGE,{"disambiguationData":[TD([[makeQuery(id+"F0.imprint","INTERSECT",VERTEX,{"disambiguationData":[OD(0.0)],"derivedFrom":[subQ0,subQ1]}),1.0]])],"derivedFrom":subQ0})])]}),makeQuery(id+"F3.opExtrude","SWEPT_FACE",FACE,{"disambiguationData":[OSD([sQuery(id+"F2.wireOp",EDGE,"E14.9.0")])]})]});}
            var Q10;
            {var subQ0=sQuery(id+"F0.wireOp",EDGE,"E4.2.0");var subQ1=sQuery(id+"F0.wireOp",EDGE,"E6");Q10=makeQuery(id+"F3.boolean.opBoolean","INTERSECT",EDGE,{"derivedFrom":[makeQuery(id+"F1.opExtrude","SWEPT_FACE",FACE,{"disambiguationData":[OSD([subQ0]),TDD([makeQuery(id+"F0.imprint","IMPRINT",EDGE,{"disambiguationData":[TD([[makeQuery(id+"F0.imprint","INTERSECT",VERTEX,{"disambiguationData":[OD(0.0)],"derivedFrom":[subQ0,subQ1]}),1.0]])],"derivedFrom":subQ0})])]}),makeQuery(id+"F3.opExtrude","SWEPT_FACE",FACE,{"disambiguationData":[OSD([sQuery(id+"F2.wireOp",EDGE,"E14.2.0")])]})]});}
            var Q11;
            {var subQ0=sQuery(id+"F0.wireOp",EDGE,"E4.1.0");var subQ1=sQuery(id+"F0.wireOp",EDGE,"E6");Q11=makeQuery(id+"F3.boolean.opBoolean","INTERSECT",EDGE,{"derivedFrom":[makeQuery(id+"F1.opExtrude","SWEPT_FACE",FACE,{"disambiguationData":[OSD([subQ0]),TDD([makeQuery(id+"F0.imprint","IMPRINT",EDGE,{"disambiguationData":[TD([[makeQuery(id+"F0.imprint","INTERSECT",VERTEX,{"disambiguationData":[OD(0.0)],"derivedFrom":[subQ0,subQ1]}),1.0]])],"derivedFrom":subQ0})])]}),makeQuery(id+"F3.opExtrude","SWEPT_FACE",FACE,{"disambiguationData":[OSD([sQuery(id+"F2.wireOp",EDGE,"E14.1.0")])]})]});}
            var Q12;
            {var subQ0=sQuery(id+"F0.wireOp",EDGE,"E3");var subQ1=sQuery(id+"F0.wireOp",EDGE,"E6");Q12=makeQuery(id+"F3.boolean.opBoolean","INTERSECT",EDGE,{"derivedFrom":[makeQuery(id+"F1.opExtrude","SWEPT_FACE",FACE,{"disambiguationData":[OSD([subQ0]),TDD([makeQuery(id+"F0.imprint","IMPRINT",EDGE,{"disambiguationData":[TD([[makeQuery(id+"F0.imprint","INTERSECT",VERTEX,{"disambiguationData":[OD(0.0)],"derivedFrom":[subQ0,subQ1]}),1.0]])],"derivedFrom":subQ0})])]}),makeQuery(id+"F3.opExtrude","SWEPT_FACE",FACE,{"disambiguationData":[OSD([sQuery(id+"F2.wireOp",EDGE,"E13.left")])]})]});}
            var Q13;
            {var subQ0=sQuery(id+"F0.wireOp",EDGE,"E4.9.0");var subQ1=sQuery(id+"F0.wireOp",EDGE,"E6");Q13=makeQuery(id+"F3.boolean.opBoolean","INTERSECT",EDGE,{"derivedFrom":[makeQuery(id+"F1.opExtrude","SWEPT_FACE",FACE,{"disambiguationData":[OSD([subQ0]),TDD([makeQuery(id+"F0.imprint","IMPRINT",EDGE,{"disambiguationData":[TD([[makeQuery(id+"F0.imprint","INTERSECT",VERTEX,{"disambiguationData":[OD(0.0)],"derivedFrom":[subQ0,subQ1]}),1.0]])],"derivedFrom":subQ0})])]}),makeQuery(id+"F3.opExtrude","SWEPT_FACE",FACE,{"disambiguationData":[OSD([sQuery(id+"F2.wireOp",EDGE,"E14.9.1")])]})]});}
            var Q14;
            {var subQ0=sQuery(id+"F0.wireOp",EDGE,"E4.8.0");var subQ1=sQuery(id+"F0.wireOp",EDGE,"E6");Q14=makeQuery(id+"F3.boolean.opBoolean","INTERSECT",EDGE,{"derivedFrom":[makeQuery(id+"F1.opExtrude","SWEPT_FACE",FACE,{"disambiguationData":[OSD([subQ0]),TDD([makeQuery(id+"F0.imprint","IMPRINT",EDGE,{"disambiguationData":[TD([[makeQuery(id+"F0.imprint","INTERSECT",VERTEX,{"disambiguationData":[OD(0.0)],"derivedFrom":[subQ0,subQ1]}),1.0]])],"derivedFrom":subQ0})])]}),makeQuery(id+"F3.opExtrude","SWEPT_FACE",FACE,{"disambiguationData":[OSD([sQuery(id+"F2.wireOp",EDGE,"E14.8.0")])]})]});}
            var Q15;
            {var subQ0=sQuery(id+"F0.wireOp",EDGE,"E4.8.0");var subQ1=sQuery(id+"F0.wireOp",EDGE,"E6");Q15=makeQuery(id+"F3.boolean.opBoolean","INTERSECT",EDGE,{"derivedFrom":[makeQuery(id+"F1.opExtrude","SWEPT_FACE",FACE,{"disambiguationData":[OSD([subQ0]),TDD([makeQuery(id+"F0.imprint","IMPRINT",EDGE,{"disambiguationData":[TD([[makeQuery(id+"F0.imprint","INTERSECT",VERTEX,{"disambiguationData":[OD(0.0)],"derivedFrom":[subQ0,subQ1]}),1.0]])],"derivedFrom":subQ0})])]}),makeQuery(id+"F3.opExtrude","SWEPT_FACE",FACE,{"disambiguationData":[OSD([sQuery(id+"F2.wireOp",EDGE,"E14.8.1")])]})]});}
            var Q16;
            {var subQ0=sQuery(id+"F0.wireOp",EDGE,"E4.6.0");var subQ1=sQuery(id+"F0.wireOp",EDGE,"E6");Q16=makeQuery(id+"F3.boolean.opBoolean","INTERSECT",EDGE,{"derivedFrom":[makeQuery(id+"F1.opExtrude","SWEPT_FACE",FACE,{"disambiguationData":[OSD([subQ0]),TDD([makeQuery(id+"F0.imprint","IMPRINT",EDGE,{"disambiguationData":[TD([[makeQuery(id+"F0.imprint","INTERSECT",VERTEX,{"disambiguationData":[OD(0.0)],"derivedFrom":[subQ0,subQ1]}),1.0]])],"derivedFrom":subQ0})])]}),makeQuery(id+"F3.opExtrude","SWEPT_FACE",FACE,{"disambiguationData":[OSD([sQuery(id+"F2.wireOp",EDGE,"E14.6.1")])]})]});}
            var Q17;
            {var subQ0=sQuery(id+"F0.wireOp",EDGE,"E4.6.0");var subQ1=sQuery(id+"F0.wireOp",EDGE,"E6");Q17=makeQuery(id+"F3.boolean.opBoolean","INTERSECT",EDGE,{"derivedFrom":[makeQuery(id+"F1.opExtrude","SWEPT_FACE",FACE,{"disambiguationData":[OSD([subQ0]),TDD([makeQuery(id+"F0.imprint","IMPRINT",EDGE,{"disambiguationData":[TD([[makeQuery(id+"F0.imprint","INTERSECT",VERTEX,{"disambiguationData":[OD(0.0)],"derivedFrom":[subQ0,subQ1]}),1.0]])],"derivedFrom":subQ0})])]}),makeQuery(id+"F3.opExtrude","SWEPT_FACE",FACE,{"disambiguationData":[OSD([sQuery(id+"F2.wireOp",EDGE,"E14.6.0")])]})]});}
            var Q18;
            {var subQ0=sQuery(id+"F0.wireOp",EDGE,"E4.7.0");var subQ1=sQuery(id+"F0.wireOp",EDGE,"E6");Q18=makeQuery(id+"F3.boolean.opBoolean","INTERSECT",EDGE,{"derivedFrom":[makeQuery(id+"F1.opExtrude","SWEPT_FACE",FACE,{"disambiguationData":[OSD([subQ0]),TDD([makeQuery(id+"F0.imprint","IMPRINT",EDGE,{"disambiguationData":[TD([[makeQuery(id+"F0.imprint","INTERSECT",VERTEX,{"disambiguationData":[OD(0.0)],"derivedFrom":[subQ0,subQ1]}),1.0]])],"derivedFrom":subQ0})])]}),makeQuery(id+"F3.opExtrude","SWEPT_FACE",FACE,{"disambiguationData":[OSD([sQuery(id+"F2.wireOp",EDGE,"E14.7.1")])]})]});}
            var Q19;
            {var subQ0=sQuery(id+"F0.wireOp",EDGE,"E4.7.0");var subQ1=sQuery(id+"F0.wireOp",EDGE,"E6");Q19=makeQuery(id+"F3.boolean.opBoolean","INTERSECT",EDGE,{"derivedFrom":[makeQuery(id+"F1.opExtrude","SWEPT_FACE",FACE,{"disambiguationData":[OSD([subQ0]),TDD([makeQuery(id+"F0.imprint","IMPRINT",EDGE,{"disambiguationData":[TD([[makeQuery(id+"F0.imprint","INTERSECT",VERTEX,{"disambiguationData":[OD(0.0)],"derivedFrom":[subQ0,subQ1]}),1.0]])],"derivedFrom":subQ0})])]}),makeQuery(id+"F3.opExtrude","SWEPT_FACE",FACE,{"disambiguationData":[OSD([sQuery(id+"F2.wireOp",EDGE,"E14.7.0")])]})]});}
            fillet(context, id + "F4", {"entities" : qUnion([Q0, Q1, Q2, Q3, Q4, Q5, Q6, Q7, Q8, Q9, Q10, Q11, Q12, Q13, Q14, Q15, Q16, Q17, Q18, Q19]), "radius" : 1 * mm, "tangentPropagation" : true, "allowEdgeOverflow" : false});
        }
    });
